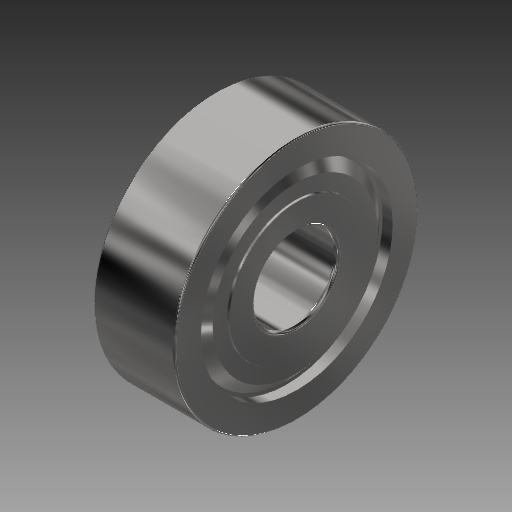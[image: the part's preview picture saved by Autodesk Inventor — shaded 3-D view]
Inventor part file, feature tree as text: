
AUTODESK INVENTOR PART (.ipt)
format: ipt  version: 2017.1 (Build 211199000, 199)  size: 706,048 bytes
history: native  units: in
note: dims shown in document units (in); Inventor stores cm internally (conversion verified against a paired STEP export)
features: other x11, imported_body x10, extrude x1, fillet x1, sketch x1
ambient origin geometry x8: Origin, YZ Plane, XZ Plane, XY Plane, X Axis, Y Axis, Z Axis, Center Point
bodies: Body1 (feature_tree), Body2 (feature_tree), Body3 (feature_tree), Body4 (feature_tree), Body5 (feature_tree), Body6 (feature_tree), Body7 (feature_tree), Body8 (feature_tree), Body9 (feature_tree), Body10 (feature_tree)
feature tree (24):
  other  "1614ZZ"
  other  "1614ZZ1"
  extrude  "Extrusion1"  Depth=0.01in
  fillet  "Fillet1"  [1 undecoded]
  other  "1614ZZ_1"
  other  "1614ZZ_2"
  other  "1614ZZ_3"
  other  "1614ZZ_4"
  other  "1614ZZ_5"
  other  "1614ZZ_6"
  other  "1614ZZ_7"
  other  "1614ZZ_8"
  other  "1614ZZ_9"
  imported_body  "Base1"
  imported_body  "Base2"
  imported_body  "Base3"
  imported_body  "Base4"
  imported_body  "Base5"
  imported_body  "Base6"
  imported_body  "Base7"
  imported_body  "Base8"
  imported_body  "Base9"
  imported_body  "Base10"
  sketch  "Sketch1"  dims[d0=1.0in d1=0.0in d2=0.01in]
note: 1 required parameter value undecoded (feature->parameter linkage not recoverable at this tier; creation-order binding heuristic only, values carry confidence <= 0.55)
